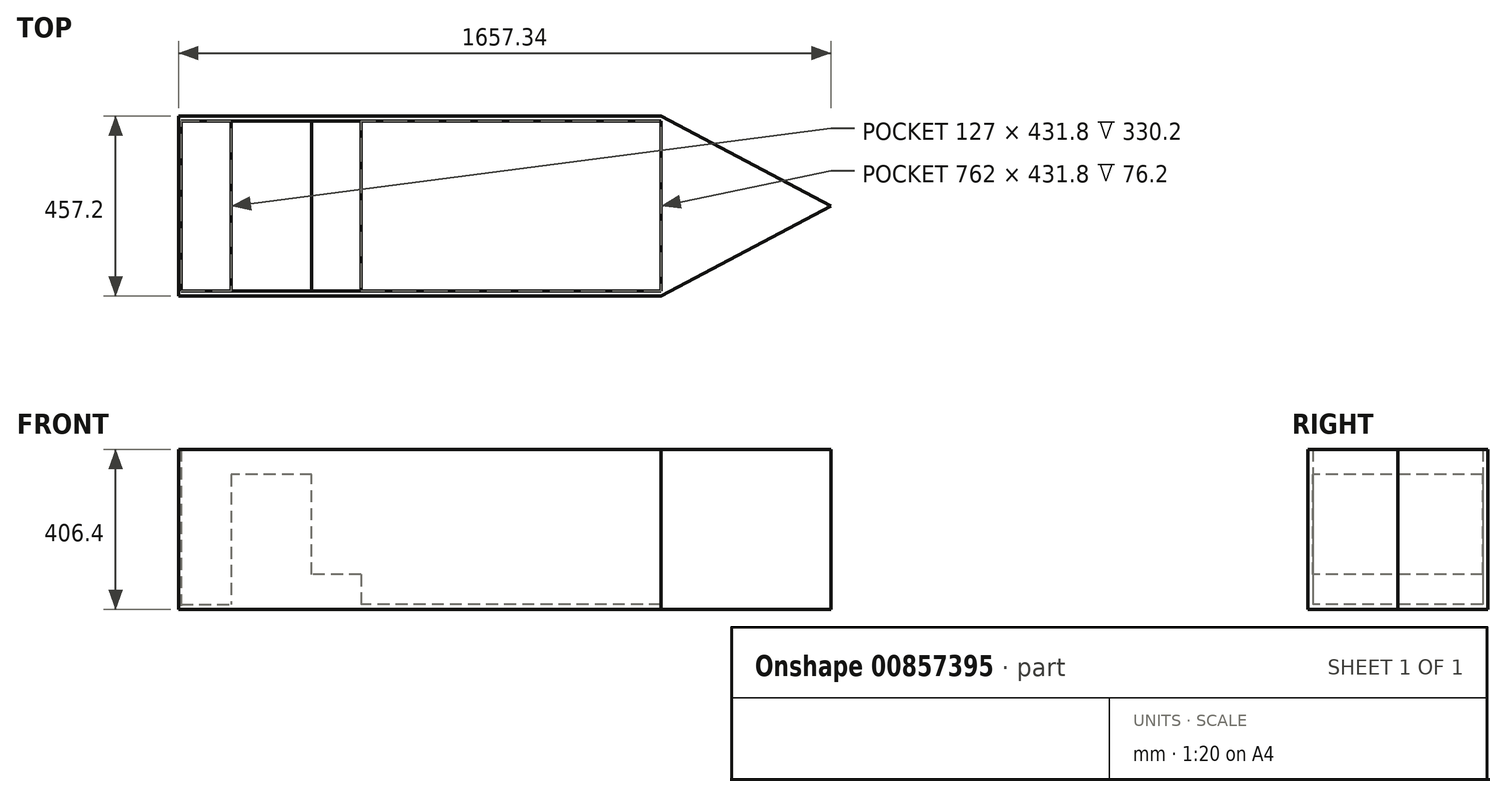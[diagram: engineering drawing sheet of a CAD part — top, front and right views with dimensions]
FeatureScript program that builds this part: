
annotation { "Feature Type Name" : "Feature", "Feature Type Description" : "" }
export const myFeature = defineFeature(function(context is Context, id is Id, definition is map)
    precondition{}
    {
        {
            var Q0;
            Q0=qCreatedBy(makeId("Top.planeOp"),FACE);
            var sketch = newSketch(context, id + "F0", { "sketchPlane" : qUnion([Q0])});
            skLineSegment(sketch, "E0", {"start": v(0, 0) * mm, "end": v(1219.2, 0) * mm});
            skLineSegment(sketch, "E1", {"start": v(1243.19, 12.7) * mm, "end": v(0, 12.7) * mm});
            skLineSegment(sketch, "E2", {"start": v(0, 12.7) * mm, "end": v(0, 0) * mm});
            skLineSegment(sketch, "E3", {"start": v(0, 0) * mm, "end": v(0, 12.7) * mm});
            skLineSegment(sketch, "E4", {"start": v(0, 12.7) * mm, "end": v(0, 444.5) * mm});
            skLineSegment(sketch, "E5", {"start": v(0, 444.5) * mm, "end": v(1243.19, 444.5) * mm});
            skLineSegment(sketch, "E6", {"start": v(1219.2, 457.2) * mm, "end": v(0, 457.2) * mm});
            skLineSegment(sketch, "E7", {"start": v(0, 457.2) * mm, "end": v(0, 444.5) * mm});
            skLineSegment(sketch, "E8", {"start": v(0, 0) * mm, "end": v(-6.34, 0) * mm});
            skLineSegment(sketch, "E9", {"start": v(-6.34, 0) * mm, "end": v(-6.34, 456.9) * mm});
            skLineSegment(sketch, "E10", {"start": v(-6.34, 456.9) * mm, "end": v(0, 457.2) * mm});
            skLineSegment(sketch, "E11", {"start": v(1219.2, 0) * mm, "end": v(1651, 228.6) * mm});
            skLineSegment(sketch, "E12", {"start": v(1651, 228.6) * mm, "end": v(1219.2, 457.2) * mm});
            skPoint(sketch, "E13.start.orphan", {"position": v(1651, 444.5) * mm});
            skPoint(sketch, "E14.end.orphan", {"position": v(1651, 12.7) * mm});
            skLineSegment(sketch, "E15", {"start": v(1219.2, 457.2) * mm, "end": v(1219.2, 0) * mm});
            skSolve(sketch);
        }
        {
            var Q0;
            Q0 = qSketchRegion(id + "F0", true);
            extrude(context, id + "F1", {"entities" : qUnion([Q0]), "depth" : 406.4 * mm, "offsetDistance" : 25.4 * mm});
        }
        {
            var Q0;
            Q0=makeQuery(id+"F1.opExtrude","CAP_FACE",FACE,{"disambiguationData":[OSD([sQuery(id+"F0.wireOp",EDGE,"E1"),sQuery(id+"F0.wireOp",EDGE,"E4"),sQuery(id+"F0.wireOp",EDGE,"E5"),sQuery(id+"F0.wireOp",EDGE,"E6"),sQuery(id+"F0.wireOp",EDGE,"E8"),sQuery(id+"F0.wireOp",EDGE,"E9"),sQuery(id+"F0.wireOp",EDGE,"E10"),sQuery(id+"F0.wireOp",EDGE,"E0"),sQuery(id+"F0.wireOp",EDGE,"E11"),sQuery(id+"F0.wireOp",EDGE,"E12"),sQuery(id+"F0.wireOp",EDGE,"E15")])],"isStart":true});
            var sketch = newSketch(context, id + "F2", { "sketchPlane" : qUnion([Q0])});
            skLineSegment(sketch, "E16", {"start": v(0, -12.7) * mm, "end": v(0, -444.5) * mm});
            skLineSegment(sketch, "E17", {"start": v(0, -444.5) * mm, "end": v(1219.2, -444.5) * mm});
            skLineSegment(sketch, "E18", {"start": v(1219.2, -444.5) * mm, "end": v(1219.2, -12.7) * mm});
            skLineSegment(sketch, "E19", {"start": v(1219.2, -12.7) * mm, "end": v(0, -12.7) * mm});
            skSolve(sketch);
        }
        {
            var Q0;
            Q0 = qSketchRegion(id + "F2", true);
            extrude(context, id + "F3", {"entities" : qUnion([Q0]), "operationType" : NewBodyOperationType.ADD, "oppositeDirection" : true, "depth" : 12.7 * mm, "offsetDistance" : 25.4 * mm});
        }
        {
            var Q0;
            Q0=makeQuery(id+"F3.opExtrude","CAP_FACE",FACE,{"disambiguationData":[OSD([sQuery(id+"F2.wireOp",EDGE,"E16"),sQuery(id+"F2.wireOp",EDGE,"E17"),sQuery(id+"F2.wireOp",EDGE,"E18"),sQuery(id+"F2.wireOp",EDGE,"E19")])],"isStart":false});
            var sketch = newSketch(context, id + "F4", { "sketchPlane" : qUnion([Q0])});
            skLineSegment(sketch, "E20", {"start": v(0, 444.5) * mm, "end": v(127, 444.5) * mm});
            skLineSegment(sketch, "E21", {"start": v(127, 444.5) * mm, "end": v(127, 12.7) * mm});
            skLineSegment(sketch, "E22", {"start": v(127, 12.7) * mm, "end": v(330.2, 12.7) * mm});
            skLineSegment(sketch, "E23", {"start": v(330.2, 12.7) * mm, "end": v(330.2, 444.5) * mm});
            skLineSegment(sketch, "E24", {"start": v(330.2, 444.5) * mm, "end": v(127, 444.5) * mm});
            skLineSegment(sketch, "E25", {"start": v(330.2, 444.5) * mm, "end": v(457.2, 444.5) * mm});
            skLineSegment(sketch, "E26", {"start": v(457.2, 444.5) * mm, "end": v(457.2, 12.7) * mm});
            skLineSegment(sketch, "E27", {"start": v(457.2, 12.7) * mm, "end": v(330.2, 12.7) * mm});
            skSolve(sketch);
        }
        {
            var Q0;
            Q0 = qSketchRegion(id + "F4", true);
            extrude(context, id + "F5", {"entities" : qUnion([Q0]), "operationType" : NewBodyOperationType.ADD, "depth" : 330.2 * mm, "offsetDistance" : 25.4 * mm});
        }
        {
            var Q0;
            Q0=makeQuery(id+"F5.opExtrude","CAP_FACE",FACE,{"disambiguationData":[OSD([sQuery(id+"F4.wireOp",EDGE,"E21"),sQuery(id+"F4.wireOp",EDGE,"E22"),sQuery(id+"F4.wireOp",EDGE,"E24"),sQuery(id+"F4.wireOp",EDGE,"E25"),sQuery(id+"F4.wireOp",EDGE,"E26"),sQuery(id+"F4.wireOp",EDGE,"E27")])],"isStart":false});
            var sketch = newSketch(context, id + "F6", { "sketchPlane" : qUnion([Q0])});
            skLineSegment(sketch, "E28", {"start": v(457.2, 444.5) * mm, "end": v(332.2, 444.5) * mm});
            skLineSegment(sketch, "E29", {"start": v(332.2, 444.5) * mm, "end": v(332.2, 12.7) * mm});
            skLineSegment(sketch, "E30", {"start": v(332.2, 12.7) * mm, "end": v(457.2, 12.7) * mm});
            skLineSegment(sketch, "E31", {"start": v(457.2, 12.7) * mm, "end": v(457.2, 444.5) * mm});
            skSolve(sketch);
        }
        {
            var Q0;
            Q0 = qSketchRegion(id + "F6", true);
            extrude(context, id + "F7", {"entities" : qUnion([Q0]), "operationType" : NewBodyOperationType.REMOVE, "oppositeDirection" : true, "depth" : 254 * mm, "offsetDistance" : 25.4 * mm});
        }
    });
